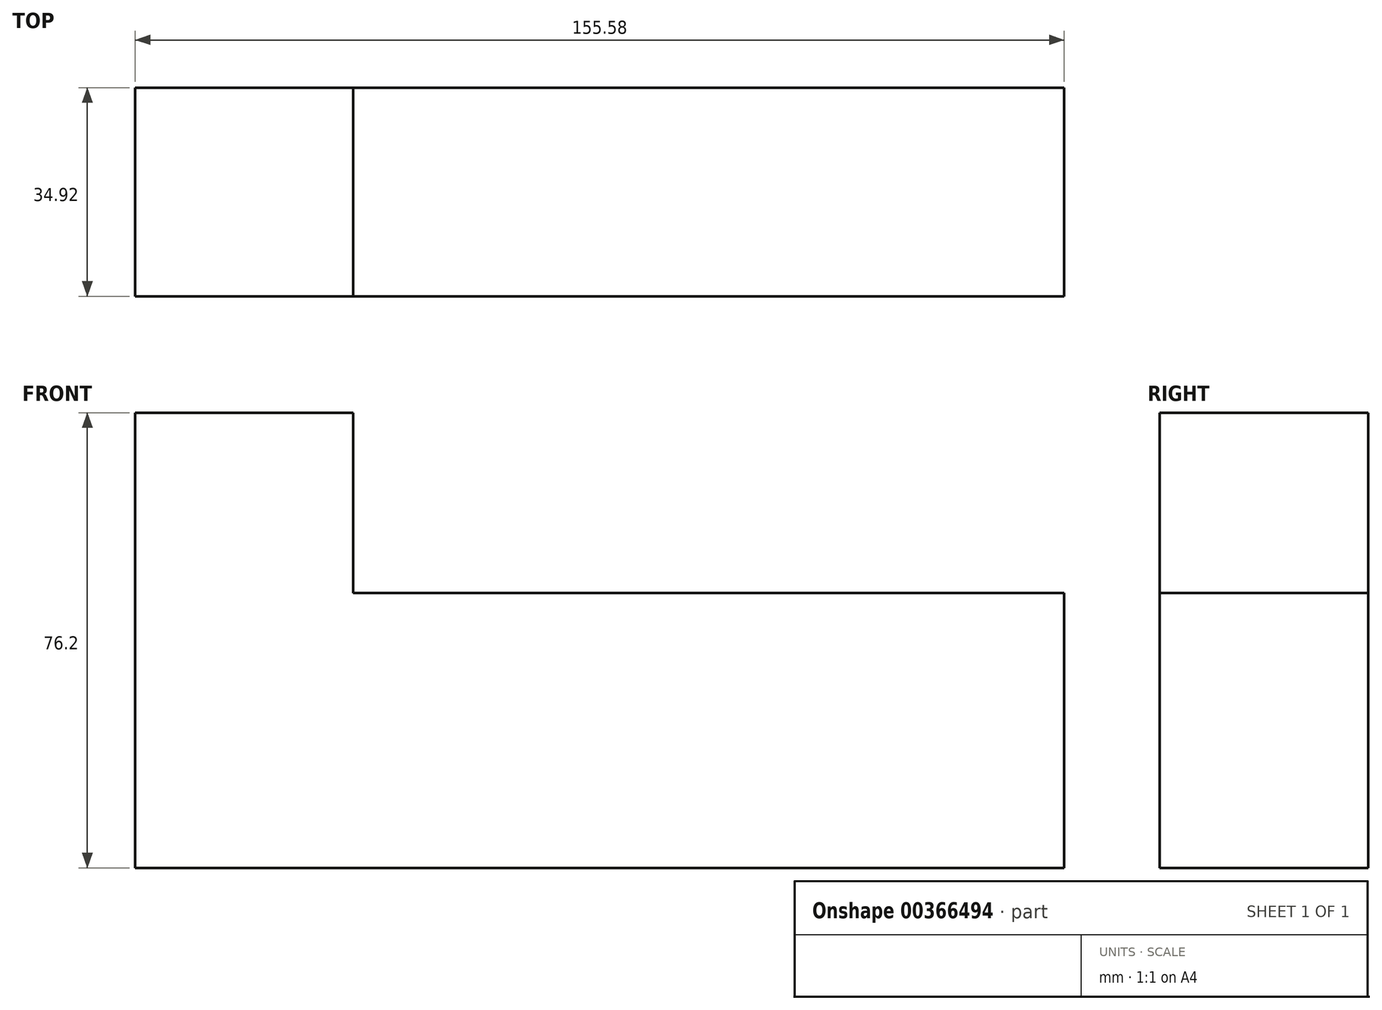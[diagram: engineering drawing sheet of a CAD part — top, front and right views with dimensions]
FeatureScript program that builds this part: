
annotation { "Feature Type Name" : "Feature", "Feature Type Description" : "" }
export const myFeature = defineFeature(function(context is Context, id is Id, definition is map)
    precondition{}
    {
        {
            var Q0;
            Q0=qCreatedBy(makeId("Front.planeOp"),FACE);
            var sketch = newSketch(context, id + "F0", { "sketchPlane" : qUnion([Q0])});
            skLineSegment(sketch, "E0.bottom", {"start": v(77.79, 23.02) * mm, "end": v(-77.79, 23.02) * mm});
            skLineSegment(sketch, "E0.top", {"start": v(77.79, -23.02) * mm, "end": v(-77.79, -23.02) * mm});
            skLineSegment(sketch, "E0.left", {"start": v(77.79, 23.02) * mm, "end": v(77.79, -23.02) * mm});
            skLineSegment(sketch, "E0.right", {"start": v(-77.79, 23.02) * mm, "end": v(-77.79, -23.02) * mm});
            skPoint(sketch, "E0.middle", {"position": v(0, 0) * mm});
            skLineSegment(sketch, "E1.bottom", {"start": v(-77.79, 23.02) * mm, "end": v(-41.28, 23.02) * mm});
            skLineSegment(sketch, "E1.top", {"start": v(-77.79, 53.18) * mm, "end": v(-41.28, 53.18) * mm});
            skLineSegment(sketch, "E1.left", {"start": v(-77.79, 23.02) * mm, "end": v(-77.79, 53.18) * mm});
            skLineSegment(sketch, "E1.right", {"start": v(-41.28, 23.02) * mm, "end": v(-41.28, 53.18) * mm});
            skSolve(sketch);
        }
        {
            var Q0;
            Q0 = qSketchRegion(id + "F0", true);
            extrude(context, id + "F1", {"entities" : qUnion([Q0]), "endBound" : BoundingType.SYMMETRIC, "depth" : 34.92 * mm});
        }
    });
